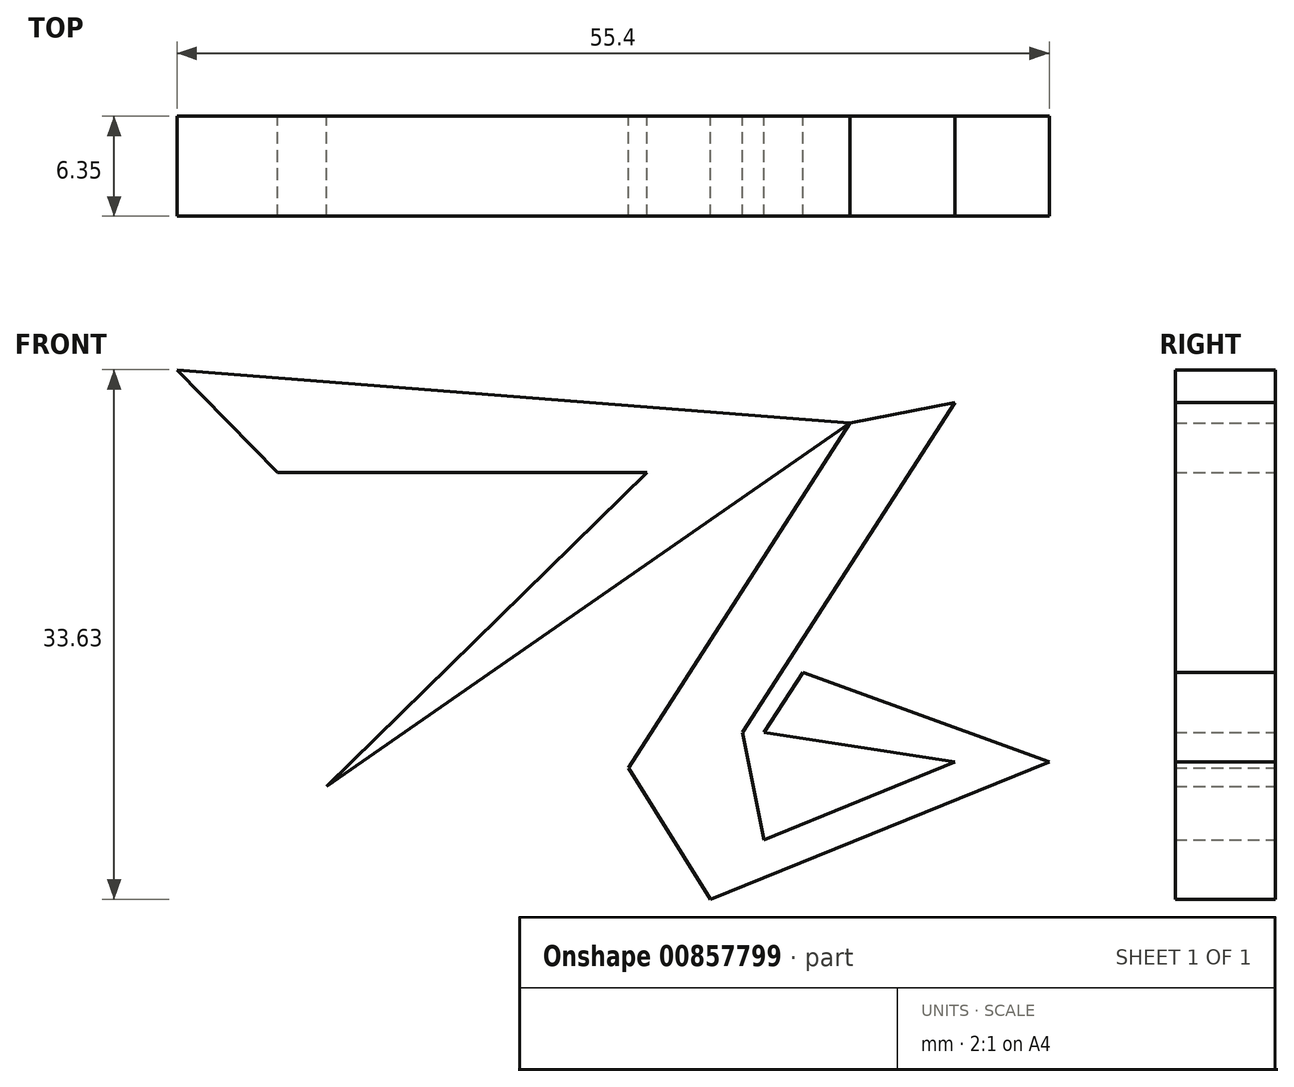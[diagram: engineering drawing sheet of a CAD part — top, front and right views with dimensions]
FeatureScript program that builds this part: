
annotation { "Feature Type Name" : "Feature", "Feature Type Description" : "" }
export const myFeature = defineFeature(function(context is Context, id is Id, definition is map)
    precondition{}
    {
        {
            var Q0;
            Q0=qCreatedBy(makeId("Front.planeOp"),FACE);
            var sketch = newSketch(context, id + "F0", { "sketchPlane" : qUnion([Q0])});
            skLineSegment(sketch, "E0", {"start": v(-50.75, 14.8) * mm, "end": v(-30.41, 34.74) * mm});
            skLineSegment(sketch, "E1", {"start": v(-30.41, 34.74) * mm, "end": v(-53.87, 34.74) * mm});
            skLineSegment(sketch, "E2", {"start": v(-53.87, 34.74) * mm, "end": v(-60.26, 41.26) * mm});
            skLineSegment(sketch, "E3", {"start": v(-60.26, 41.26) * mm, "end": v(-17.5, 37.87) * mm});
            skLineSegment(sketch, "E4", {"start": v(-17.5, 37.87) * mm, "end": v(-50.75, 14.8) * mm});
            skLineSegment(sketch, "E5", {"start": v(-17.5, 37.87) * mm, "end": v(-31.58, 15.97) * mm});
            skLineSegment(sketch, "E6", {"start": v(-17.5, 37.87) * mm, "end": v(-10.86, 39.17) * mm});
            skLineSegment(sketch, "E7", {"start": v(-10.86, 39.17) * mm, "end": v(-24.33, 18.22) * mm});
            skLineSegment(sketch, "E8", {"start": v(-24.33, 18.22) * mm, "end": v(-22.98, 11.4) * mm});
            skLineSegment(sketch, "E9", {"start": v(-22.98, 11.4) * mm, "end": v(-10.86, 16.36) * mm});
            skLineSegment(sketch, "E10", {"start": v(-10.86, 16.36) * mm, "end": v(-22.98, 18.22) * mm});
            skLineSegment(sketch, "E11", {"start": v(-22.98, 18.22) * mm, "end": v(-20.52, 22.05) * mm});
            skLineSegment(sketch, "E12", {"start": v(-20.52, 22.05) * mm, "end": v(-4.86, 16.36) * mm});
            skLineSegment(sketch, "E13", {"start": v(-4.86, 16.36) * mm, "end": v(-26.37, 7.63) * mm});
            skLineSegment(sketch, "E14", {"start": v(-26.37, 7.63) * mm, "end": v(-31.58, 15.97) * mm});
            skSolve(sketch);
        }
        {
            var Q0;
            Q0 = qSketchRegion(id + "F0", true);
            extrude(context, id + "F1", {"entities" : qUnion([Q0]), "depth" : 6.35 * mm, "offsetDistance" : 25.4 * mm});
        }
    });
